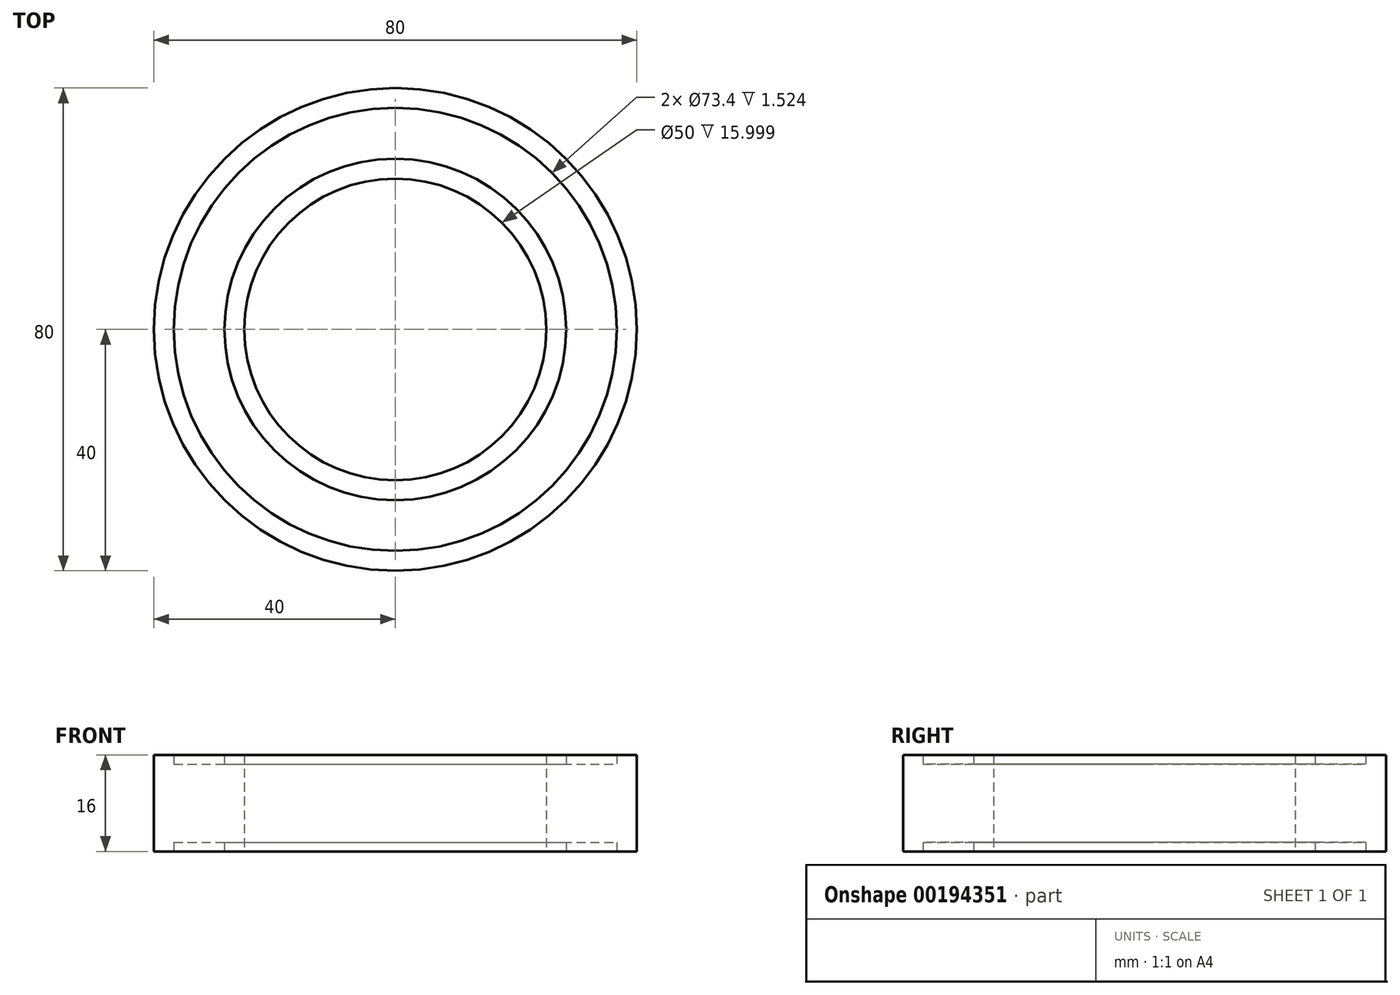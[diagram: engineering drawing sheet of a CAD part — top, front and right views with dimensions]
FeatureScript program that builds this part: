
annotation { "Feature Type Name" : "Feature", "Feature Type Description" : "" }
export const myFeature = defineFeature(function(context is Context, id is Id, definition is map)
    precondition{}
    {
        {
            var Q0;
            Q0=qCreatedBy(makeId("Right.planeOp"),FACE);
            var sketch = newSketch(context, id + "F0", { "sketchPlane" : qUnion([Q0])});
            skLineSegment(sketch, "E0", {"start": v(0, 0) * mm, "end": v(0, 16) * mm, "construction": true});
            skLineSegment(sketch, "E1", {"start": v(-25, 0) * mm, "end": v(-25, 16) * mm});
            skLineSegment(sketch, "E2", {"start": v(-25, 16) * mm, "end": v(-28.3, 16) * mm});
            skLineSegment(sketch, "E3", {"start": v(-28.3, 16) * mm, "end": v(-28.3, 14.48) * mm});
            skLineSegment(sketch, "E4", {"start": v(-28.3, 14.48) * mm, "end": v(-36.7, 14.48) * mm});
            skLineSegment(sketch, "E5", {"start": v(-36.7, 14.48) * mm, "end": v(-36.7, 16) * mm});
            skLineSegment(sketch, "E6", {"start": v(-36.7, 16) * mm, "end": v(-40, 16) * mm});
            skLineSegment(sketch, "E7", {"start": v(-40, 16) * mm, "end": v(-40, 0) * mm});
            skLineSegment(sketch, "E8", {"start": v(-40, 0) * mm, "end": v(-36.7, 0) * mm});
            skLineSegment(sketch, "E9", {"start": v(-36.7, 0) * mm, "end": v(-36.7, 1.52) * mm});
            skLineSegment(sketch, "E10", {"start": v(-36.7, 1.52) * mm, "end": v(-28.3, 1.52) * mm});
            skLineSegment(sketch, "E11", {"start": v(-28.3, 1.52) * mm, "end": v(-28.3, 0) * mm});
            skLineSegment(sketch, "E12", {"start": v(-28.3, 0) * mm, "end": v(-25, 0) * mm});
            skSolve(sketch);
        }
        {
            var Q0;
            Q0=qSketchRegion(id+"F0",true);
            var Q1;
            Q1=sQuery(id+"F0.wireOp",EDGE,"E0");
            revolve(context, id + "F1", {"entities" : qUnion([Q0]), "axis" : qUnion([Q1]), "revolveType" : RevolveType.FULL});
        }
    });
